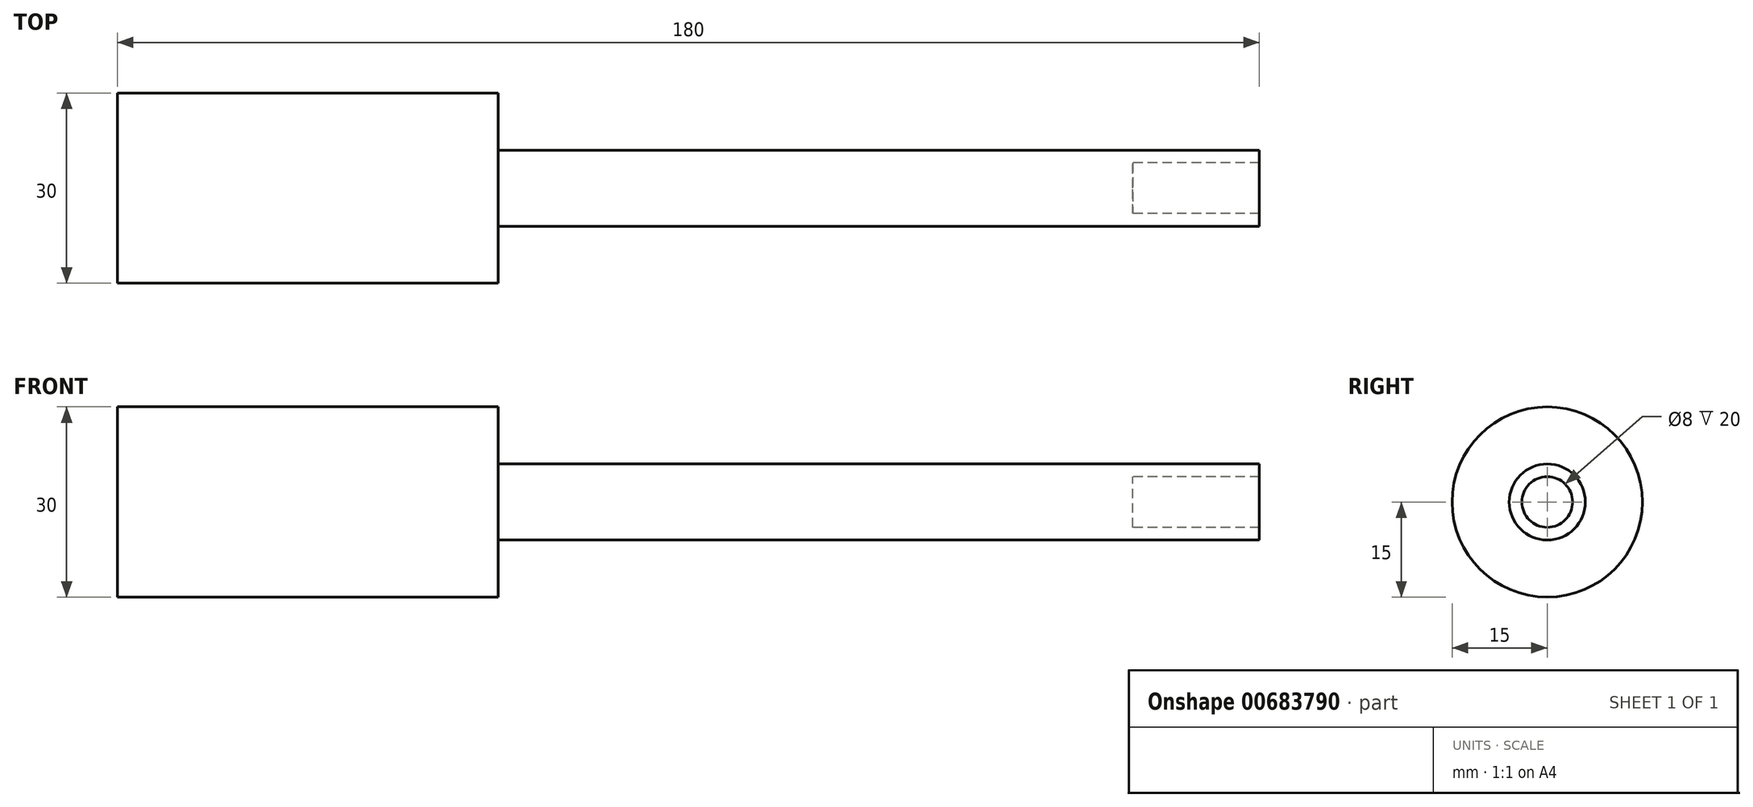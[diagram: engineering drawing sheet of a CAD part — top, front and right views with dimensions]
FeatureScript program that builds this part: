
annotation { "Feature Type Name" : "Feature", "Feature Type Description" : "" }
export const myFeature = defineFeature(function(context is Context, id is Id, definition is map)
    precondition{}
    {
        {
            var Q0;
            Q0=qCreatedBy(makeId("Right.planeOp"),FACE);
            var sketch = newSketch(context, id + "F0", { "sketchPlane" : qUnion([Q0])});
            skCircle(sketch, "E0", {"center": v(0, 0) * mm, "radius": 15 * mm});
            skCircle(sketch, "E1", {"center": v(0, 0) * mm, "radius": 6 * mm});
            skCircle(sketch, "E2", {"center": v(0, 0) * mm, "radius": 4 * mm});
            skSolve(sketch);
        }
        {
            var Q0;
            Q0=makeQuery(id+"F0.imprint","IMPRINT",FACE,{"disambiguationData":[TD([[makeQuery(id+"F0.imprint","IMPRINT",EDGE,{"derivedFrom":sQuery(id+"F0.wireOp",EDGE,"E0")}),1.0]])]});
            var Q1;
            Q1=makeQuery(id+"F0.imprint","IMPRINT",FACE,{"disambiguationData":[TD([[makeQuery(id+"F0.imprint","IMPRINT",EDGE,{"derivedFrom":sQuery(id+"F0.wireOp",EDGE,"E1")}),1.0]])]});
            var Q2;
            Q2=makeQuery(id+"F0.imprint","IMPRINT",FACE,{"disambiguationData":[TD([[makeQuery(id+"F0.imprint","IMPRINT",EDGE,{"derivedFrom":sQuery(id+"F0.wireOp",EDGE,"E2")}),1.0]])]});
            extrude(context, id + "F1", {"entities" : qUnion([Q0, Q1, Q2]), "depth" : 60 * mm, "offsetDistance" : 25 * mm});
        }
        {
            var Q0;
            Q0=makeQuery(id+"F0.imprint","IMPRINT",FACE,{"disambiguationData":[TD([[makeQuery(id+"F0.imprint","IMPRINT",EDGE,{"derivedFrom":sQuery(id+"F0.wireOp",EDGE,"E1")}),1.0]])]});
            extrude(context, id + "F2", {"entities" : qUnion([Q0]), "operationType" : NewBodyOperationType.ADD, "depth" : 180 * mm, "offsetDistance" : 25 * mm});
        }
        {
            var Q0;
            Q0=makeQuery(id+"F0.imprint","IMPRINT",FACE,{"disambiguationData":[TD([[makeQuery(id+"F0.imprint","IMPRINT",EDGE,{"derivedFrom":sQuery(id+"F0.wireOp",EDGE,"E2")}),1.0]])]});
            extrude(context, id + "F3", {"entities" : qUnion([Q0]), "operationType" : NewBodyOperationType.ADD, "depth" : 160 * mm, "offsetDistance" : 25 * mm});
        }
    });
